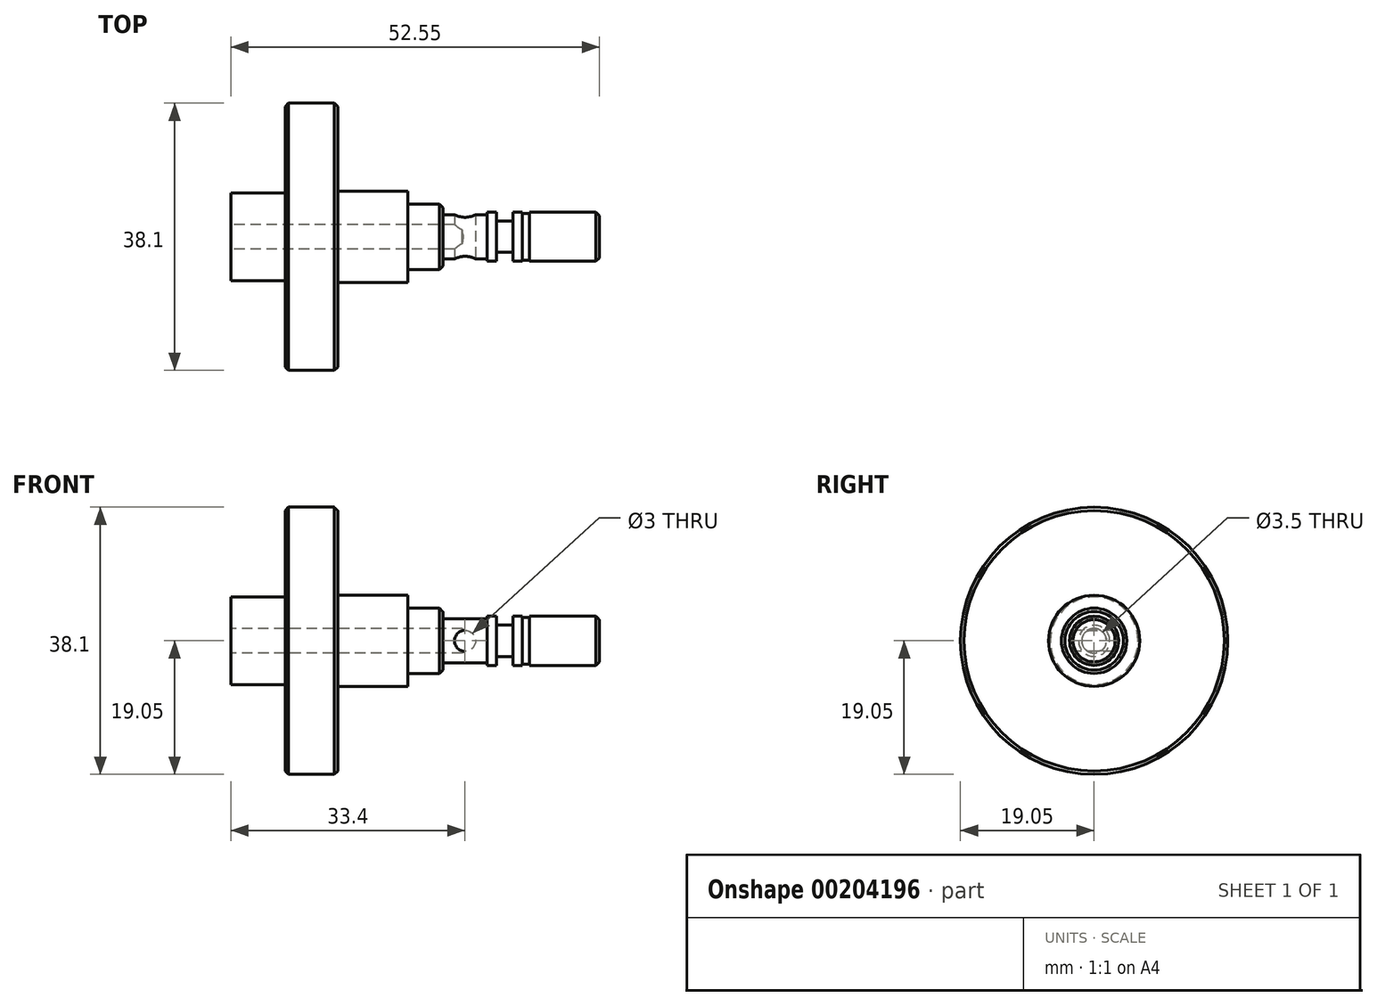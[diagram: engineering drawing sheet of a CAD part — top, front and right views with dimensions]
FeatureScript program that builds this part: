
annotation { "Feature Type Name" : "Feature", "Feature Type Description" : "" }
export const myFeature = defineFeature(function(context is Context, id is Id, definition is map)
    precondition{}
    {
        {
            var Q0;
            Q0=qCreatedBy(makeId("Front.planeOp"),FACE);
            var sketch = newSketch(context, id + "F0", { "sketchPlane" : qUnion([Q0])});
            skLineSegment(sketch, "E0", {"start": v(0, 0) * mm, "end": v(0, 6.25) * mm});
            skLineSegment(sketch, "E1", {"start": v(0, 6.25) * mm, "end": v(7.75, 6.25) * mm});
            skLineSegment(sketch, "E2", {"start": v(7.75, 6.25) * mm, "end": v(7.75, 19.05) * mm});
            skLineSegment(sketch, "E3", {"start": v(7.75, 19.05) * mm, "end": v(15.25, 19.05) * mm});
            skLineSegment(sketch, "E4", {"start": v(15.25, 19.05) * mm, "end": v(15.25, 6.5) * mm});
            skLineSegment(sketch, "E5", {"start": v(30.25, 4.66) * mm, "end": v(30.25, 3.15) * mm});
            skLineSegment(sketch, "E6", {"start": v(30.25, 3.15) * mm, "end": v(36.55, 3.15) * mm});
            skLineSegment(sketch, "E7", {"start": v(36.55, 3.15) * mm, "end": v(36.55, 3.5) * mm});
            skLineSegment(sketch, "E8", {"start": v(36.55, 3.5) * mm, "end": v(37.85, 3.5) * mm});
            skLineSegment(sketch, "E9", {"start": v(37.85, 3.5) * mm, "end": v(37.85, 2.23) * mm});
            skLineSegment(sketch, "E10", {"start": v(37.85, 2.23) * mm, "end": v(40.25, 2.23) * mm});
            skLineSegment(sketch, "E11", {"start": v(40.25, 2.23) * mm, "end": v(40.25, 3.5) * mm});
            skLineSegment(sketch, "E12", {"start": v(40.25, 3.5) * mm, "end": v(41.55, 3.5) * mm});
            skLineSegment(sketch, "E13", {"start": v(41.55, 3.5) * mm, "end": v(41.55, 3.35) * mm});
            skLineSegment(sketch, "E14", {"start": v(41.55, 3.35) * mm, "end": v(42.55, 3.35) * mm});
            skLineSegment(sketch, "E15", {"start": v(42.55, 3.35) * mm, "end": v(42.55, 3.5) * mm});
            skLineSegment(sketch, "E16", {"start": v(42.55, 3.5) * mm, "end": v(52.55, 3.5) * mm});
            skLineSegment(sketch, "E17", {"start": v(52.55, 3.5) * mm, "end": v(52.55, 0) * mm});
            skLineSegment(sketch, "E18", {"start": v(52.55, 0) * mm, "end": v(0, 0) * mm});
            skLineSegment(sketch, "E19", {"start": v(30.25, 4.66) * mm, "end": v(25.25, 4.66) * mm});
            skLineSegment(sketch, "E20", {"start": v(25.25, 4.66) * mm, "end": v(25.25, 6.5) * mm});
            skLineSegment(sketch, "E21", {"start": v(25.25, 6.5) * mm, "end": v(15.25, 6.5) * mm});
            skSolve(sketch);
        }
        {
            var Q0;
            Q0=makeQuery(id+"F0.imprint","IMPRINT",FACE,{"disambiguationData":[TD([[makeQuery(id+"F0.imprint","IMPRINT",EDGE,{"derivedFrom":sQuery(id+"F0.wireOp",EDGE,"E0")}),-1.0]])]});
            var Q1;
            Q1=sQuery(id+"F0.wireOp",EDGE,"E18");
            revolve(context, id + "F1", {"entities" : qUnion([Q0]), "axis" : qUnion([Q1]), "revolveType" : RevolveType.FULL});
        }
        {
            var Q0;
            Q0=makeQuery(id+"F1.opRevolve","SWEPT_EDGE",EDGE,{"disambiguationData":[OSD([sQuery(id+"F0.wireOp",EDGE,"E5"),sQuery(id+"F0.wireOp",EDGE,"E19")])]});
            var Q1;
            Q1=makeQuery(id+"F1.opRevolve","SWEPT_EDGE",EDGE,{"disambiguationData":[OSD([sQuery(id+"F0.wireOp",EDGE,"E2"),sQuery(id+"F0.wireOp",EDGE,"E3")])]});
            var Q2;
            Q2=makeQuery(id+"F1.opRevolve","SWEPT_EDGE",EDGE,{"disambiguationData":[OSD([sQuery(id+"F0.wireOp",EDGE,"E3"),sQuery(id+"F0.wireOp",EDGE,"E4")])]});
            var Q3;
            Q3=makeQuery(id+"F1.opRevolve","SWEPT_EDGE",EDGE,{"disambiguationData":[OSD([sQuery(id+"F0.wireOp",EDGE,"E16"),sQuery(id+"F0.wireOp",EDGE,"E17")])]});
            chamfer(context, id + "F2", {"entities" : qUnion([Q0, Q1, Q2, Q3]), "width" : .5 * mm, "tangentPropagation" : true});
        }
        {
            var Q0;
            Q0=qCreatedBy(makeId("Front.planeOp"),FACE);
            var sketch = newSketch(context, id + "F3", { "sketchPlane" : qUnion([Q0])});
            skCircle(sketch, "E22", {"center": v(33.4, 0) * mm, "radius": 1.5 * mm});
            skSolve(sketch);
        }
        {
            var Q0;
            Q0=sQuery(id+"F3.wireOp",VERTEX,"E22.center");
            var Q1;
            Q1=makeQuery(id+"F1.opRevolve","SWEPT_BODY",BODY,{"disambiguationData":[OSD([sQuery(id+"F0.wireOp",EDGE,"E0"),sQuery(id+"F0.wireOp",EDGE,"E1"),sQuery(id+"F0.wireOp",EDGE,"E2"),sQuery(id+"F0.wireOp",EDGE,"E3"),sQuery(id+"F0.wireOp",EDGE,"E4"),sQuery(id+"F0.wireOp",EDGE,"E5"),sQuery(id+"F0.wireOp",EDGE,"E6"),sQuery(id+"F0.wireOp",EDGE,"E7"),sQuery(id+"F0.wireOp",EDGE,"E8"),sQuery(id+"F0.wireOp",EDGE,"E9"),sQuery(id+"F0.wireOp",EDGE,"E10"),sQuery(id+"F0.wireOp",EDGE,"E11"),sQuery(id+"F0.wireOp",EDGE,"E12"),sQuery(id+"F0.wireOp",EDGE,"E13"),sQuery(id+"F0.wireOp",EDGE,"E14"),sQuery(id+"F0.wireOp",EDGE,"E15"),sQuery(id+"F0.wireOp",EDGE,"E16"),sQuery(id+"F0.wireOp",EDGE,"E17"),sQuery(id+"F0.wireOp",EDGE,"E18"),sQuery(id+"F0.wireOp",EDGE,"E19"),sQuery(id+"F0.wireOp",EDGE,"E20"),sQuery(id+"F0.wireOp",EDGE,"E21")])]});
            hole(context, id + "F4", {"style" : HoleStyle.SIMPLE, "endStyle" : HoleEndStyle.BLIND, "holeDiameter" : 3 * mm, "holeDepth" : 4 * mm, "startFromSketch" : true, "locations" : qUnion([Q0]), "scope" : qUnion([Q1])});
        }
        {
            var Q0;
            Q0=sQuery(id+"F3.wireOp",VERTEX,"E22.center");
            var Q1;
            Q1=makeQuery(id+"F1.opRevolve","SWEPT_BODY",BODY,{"disambiguationData":[OSD([sQuery(id+"F0.wireOp",EDGE,"E0"),sQuery(id+"F0.wireOp",EDGE,"E1"),sQuery(id+"F0.wireOp",EDGE,"E2"),sQuery(id+"F0.wireOp",EDGE,"E3"),sQuery(id+"F0.wireOp",EDGE,"E4"),sQuery(id+"F0.wireOp",EDGE,"E5"),sQuery(id+"F0.wireOp",EDGE,"E6"),sQuery(id+"F0.wireOp",EDGE,"E7"),sQuery(id+"F0.wireOp",EDGE,"E8"),sQuery(id+"F0.wireOp",EDGE,"E9"),sQuery(id+"F0.wireOp",EDGE,"E10"),sQuery(id+"F0.wireOp",EDGE,"E11"),sQuery(id+"F0.wireOp",EDGE,"E12"),sQuery(id+"F0.wireOp",EDGE,"E13"),sQuery(id+"F0.wireOp",EDGE,"E14"),sQuery(id+"F0.wireOp",EDGE,"E15"),sQuery(id+"F0.wireOp",EDGE,"E16"),sQuery(id+"F0.wireOp",EDGE,"E17"),sQuery(id+"F0.wireOp",EDGE,"E18"),sQuery(id+"F0.wireOp",EDGE,"E19"),sQuery(id+"F0.wireOp",EDGE,"E20"),sQuery(id+"F0.wireOp",EDGE,"E21")])]});
            hole(context, id + "F5", {"style" : HoleStyle.SIMPLE, "endStyle" : HoleEndStyle.BLIND, "oppositeDirection" : true, "holeDiameter" : 3 * mm, "holeDepth" : 4 * mm, "startFromSketch" : true, "locations" : qUnion([Q0]), "scope" : qUnion([Q1])});
        }
        {
            var Q0;
            Q0=makeQuery(id+"F1.opRevolve","SWEPT_FACE",FACE,{"disambiguationData":[OSD([sQuery(id+"F0.wireOp",EDGE,"E0")])]});
            var sketch = newSketch(context, id + "F6", { "sketchPlane" : qUnion([Q0])});
            skCircle(sketch, "E23", {"center": v(0, 0) * mm, "radius": 1.75 * mm});
            skSolve(sketch);
        }
        {
            var Q0;
            Q0=sQuery(id+"F6.wireOp",VERTEX,"E23.center");
            var Q1;
            Q1=makeQuery(id+"F1.opRevolve","SWEPT_BODY",BODY,{"disambiguationData":[OSD([sQuery(id+"F0.wireOp",EDGE,"E0"),sQuery(id+"F0.wireOp",EDGE,"E1"),sQuery(id+"F0.wireOp",EDGE,"E2"),sQuery(id+"F0.wireOp",EDGE,"E3"),sQuery(id+"F0.wireOp",EDGE,"E4"),sQuery(id+"F0.wireOp",EDGE,"E5"),sQuery(id+"F0.wireOp",EDGE,"E6"),sQuery(id+"F0.wireOp",EDGE,"E7"),sQuery(id+"F0.wireOp",EDGE,"E8"),sQuery(id+"F0.wireOp",EDGE,"E9"),sQuery(id+"F0.wireOp",EDGE,"E10"),sQuery(id+"F0.wireOp",EDGE,"E11"),sQuery(id+"F0.wireOp",EDGE,"E12"),sQuery(id+"F0.wireOp",EDGE,"E13"),sQuery(id+"F0.wireOp",EDGE,"E14"),sQuery(id+"F0.wireOp",EDGE,"E15"),sQuery(id+"F0.wireOp",EDGE,"E16"),sQuery(id+"F0.wireOp",EDGE,"E17"),sQuery(id+"F0.wireOp",EDGE,"E18"),sQuery(id+"F0.wireOp",EDGE,"E19"),sQuery(id+"F0.wireOp",EDGE,"E20"),sQuery(id+"F0.wireOp",EDGE,"E21")])]});
            hole(context, id + "F7", {"style" : HoleStyle.SIMPLE, "endStyle" : HoleEndStyle.BLIND, "holeDiameter" : 3.5 * mm, "holeDepth" : 33 * mm, "startFromSketch" : true, "locations" : qUnion([Q0]), "scope" : qUnion([Q1])});
        }
    });
